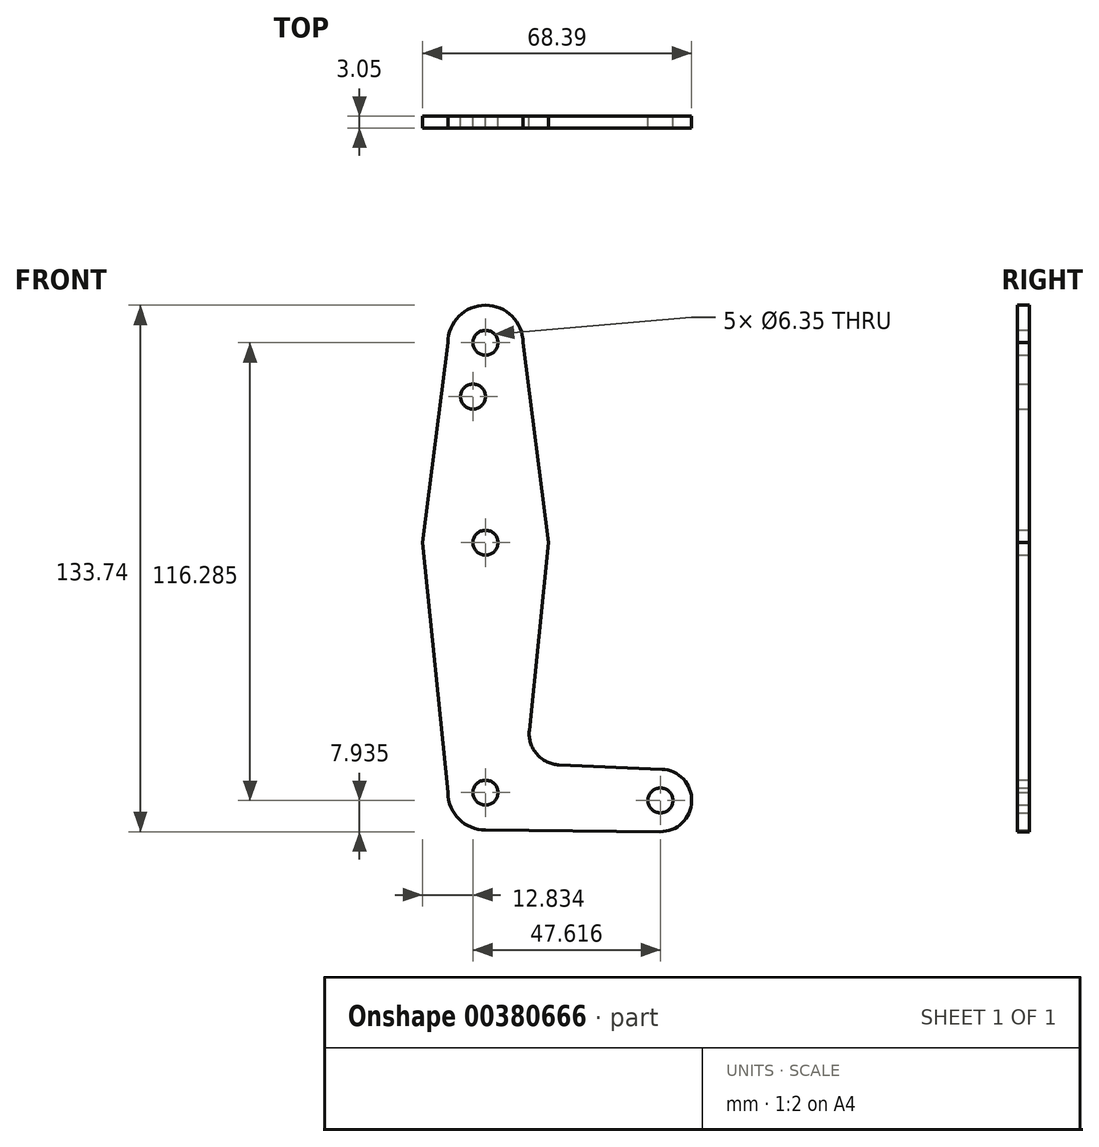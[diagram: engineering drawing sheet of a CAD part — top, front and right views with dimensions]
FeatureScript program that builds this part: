
annotation { "Feature Type Name" : "Feature", "Feature Type Description" : "" }
export const myFeature = defineFeature(function(context is Context, id is Id, definition is map)
    precondition{}
    {
        {
            var Q0;
            Q0=qCreatedBy(makeId("Front.planeOp"),FACE);
            var sketch = newSketch(context, id + "F0", { "sketchPlane" : qUnion([Q0])});
            skCircle(sketch, "E0", {"center": v(0, 50.8) * mm, "radius": 9.53 * mm});
            skCircle(sketch, "E1", {"center": v(0, 0) * mm, "radius": 15.88 * mm});
            skCircle(sketch, "E2", {"center": v(0, -63.5) * mm, "radius": 9.53 * mm});
            skCircle(sketch, "E3", {"center": v(44.45, -65.48) * mm, "radius": 7.94 * mm});
            skLineSegment(sketch, "E4", {"start": v(9.53, 50.8) * mm, "end": v(16, 0) * mm});
            skLineSegment(sketch, "E5", {"start": v(-9.53, 50.8) * mm, "end": v(-16, 0) * mm});
            skLineSegment(sketch, "E6", {"start": v(-16, 0) * mm, "end": v(-9.53, -63.5) * mm});
            skLineSegment(sketch, "E7", {"start": v(16, 0) * mm, "end": v(11.14, -47.7) * mm});
            skLineSegment(sketch, "E8", {"start": v(18.72, -56.46) * mm, "end": v(44.78, -57.55) * mm});
            skLineSegment(sketch, "E9", {"start": v(0, -73.03) * mm, "end": v(44.45, -73.42) * mm});
            skCircle(sketch, "E10", {"center": v(0, 50.8) * mm, "radius": 3.18 * mm});
            skCircle(sketch, "E11", {"center": v(0, 0) * mm, "radius": 3.18 * mm});
            skCircle(sketch, "E12", {"center": v(0, -63.5) * mm, "radius": 3.18 * mm});
            skCircle(sketch, "E13", {"center": v(44.45, -65.48) * mm, "radius": 3.18 * mm});
            skCircle(sketch, "E14", {"center": v(-3.17, 37.13) * mm, "radius": 3.18 * mm});
            skArc(sketch, "E15.filletArc", {"start": v(11.14, -47.7) * mm, "mid": v(13.04, -53.72) * mm, "end": v(18.72, -56.46) * mm});
            skSolve(sketch);
        }
        {
            var Q0;
            Q0 = qSketchRegion(id + "F0", true);
            extrude(context, id + "F1", {"entities" : qUnion([Q0]), "depth" : 3.05 * mm});
        }
    });
